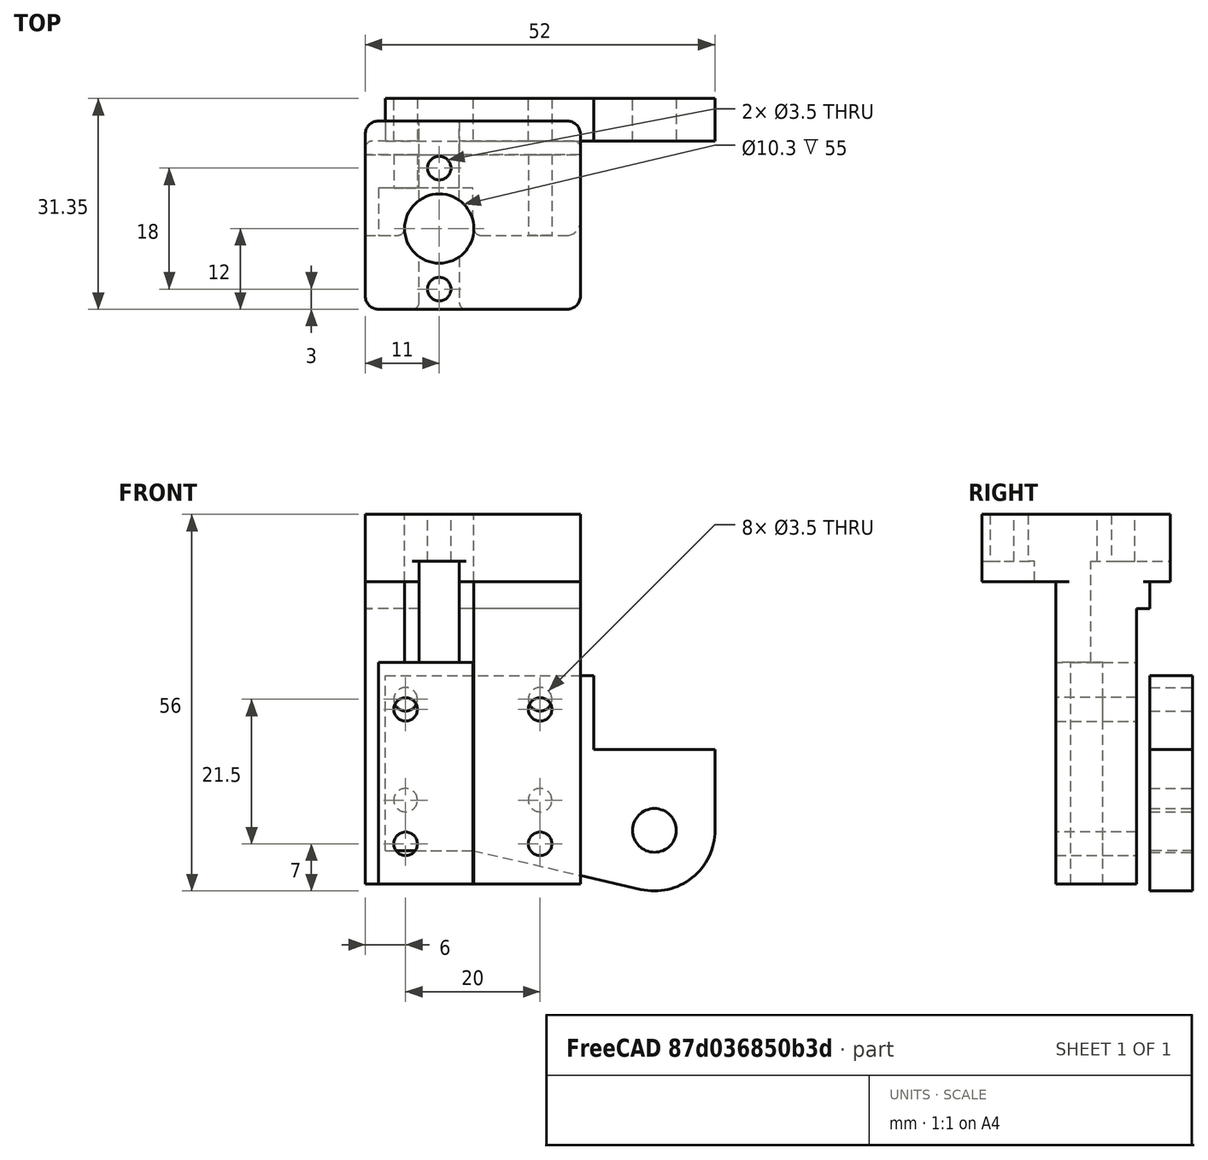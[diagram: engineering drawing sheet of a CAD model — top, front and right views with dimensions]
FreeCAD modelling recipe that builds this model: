
FCSTD DOCUMENT  (FreeCAD 0.19R)
Label: ZnutHolder_H
License: All rights reserved
LicenseURL: http://en.wikipedia.org/wiki/All_rights_reserved
objects: Sketcher::SketchObject×9, PartDesign::Pocket×6, PartDesign::Fillet×5, PartDesign::Pad×2, PartDesign::Body×2, Mesh::Feature×1
note: 37 computed .brp shape members not serialized (recipe doc carries the construction recipe); baked Part::Feature solids carry a one-line shape summary decoded from their .brp

FEATURE [Sketcher::SketchObject] Sketch
  FullyConstrained = false
  MapMode = 5
  Placement = pos=(0,0,0) rot=(1,0,0;1.5708rad)
  Support = -> [XZ_Plane]
  sketch-geometry (14):
    g0: Circle CenterX=-10 CenterY=7.5 CenterZ=0 NormalX=0 NormalY=0 NormalZ=1 AngleXU=0 Radius=1.75
    g1: Circle CenterX=10 CenterY=7.5 CenterZ=0 NormalX=0 NormalY=0 NormalZ=1 AngleXU=0 Radius=1.75
    g2: Circle CenterX=-10 CenterY=-7.5 CenterZ=0 NormalX=0 NormalY=0 NormalZ=1 AngleXU=0 Radius=1.75
    g3: Circle CenterX=10 CenterY=-7.5 CenterZ=0 NormalX=0 NormalY=0 NormalZ=1 AngleXU=0 Radius=1.75
    g4: LineSegment StartX=-13 StartY=11 StartZ=0 EndX=18 EndY=11 EndZ=0
    g5: LineSegment StartX=18 StartY=11 StartZ=0 EndX=18 EndY=0 EndZ=0
    g6: LineSegment StartX=18 StartY=0 StartZ=0 EndX=36 EndY=0 EndZ=0
    g7: LineSegment StartX=36 StartY=0 StartZ=0 EndX=36 EndY=-12 EndZ=0
    g8: LineSegment StartX=-13 StartY=-15 StartZ=0 EndX=-13 EndY=11 EndZ=0
    g9: LineSegment StartX=-13 StartY=-15 StartZ=0 EndX=0 EndY=-15 EndZ=0
    g10: LineSegment StartX=0 StartY=-15 StartZ=0 EndX=24.9743 EndY=-20.7691 EndZ=0
    g11: ArcOfCircle CenterX=27 CenterY=-12 CenterZ=0 NormalX=0 NormalY=0 NormalZ=1 AngleXU=0 Radius=9 StartAngle=4.48537 EndAngle=6.28319
    g12: Circle CenterX=27 CenterY=-12 CenterZ=0 NormalX=0 NormalY=0 NormalZ=1 AngleXU=0 Radius=3.25
    g13: LineSegment StartX=19 StartY=18.0628 StartZ=0 EndX=19 EndY=-24.6673 EndZ=0
  constraints (37):
    c: Symmetric(g0,g1,g-2)
    c: Symmetric(g3,g2,g-2)
    c: Symmetric(g3,g1,g-1)
    c: Diameter(g0) = 3.5
    c: Equal(g0,g1)
    c: Equal(g0,g2)
    c: Equal(g0,g3)
    c: Distance(g1,g0) = 20
    c: Distance(g3,g1) = 15
    c: Horizontal(g4)
    c: Coincident(g4,g5)
    c: Vertical(g5)
    c: Coincident(g5,g6)
    c: Horizontal(g6)
    c: Coincident(g6,g7)
    c: Vertical(g7)
    c: Vertical(g8)
    c: DistanceX(g4) = 18
    c: DistanceX(g4) = -13
    c: Coincident(g8,g9)
    c: PointOnObject(g9,g-2)
    c: Horizontal(g9)
    c: Coincident(g9,g10)
    c: Tangent(g7,g11) = 1.5708
    c: Coincident(g11,g7)
    c: Tangent(g11,g10) = -1.5708
    c: Coincident(g12,g11)
    c: Diameter(g12) = 6.5
    c: Diameter(g11) = 18
    c: Vertical(g13)
    c: DistanceX(g13) = 19
    c: Distance(g11,g13) = 8
    c: Distance(g11,g6) = 12
    c: PointOnObject(g5,g-1)
    c: Coincident(g8,g4)
    c: DistanceY(g4) = 11
    c: DistanceY(g8) = -15
FEATURE [PartDesign::Pad] Pad
  Direction = (1,1,1)
  Length = 6.35
  Length2 = 100
  Placement = pos=(0,0,0) rot=(1,0,0;1.5708rad)
  Profile = -> Sketch
  Type = 0
FEATURE [PartDesign::Body] Body  label="Tab"
  Group = -> [Sketch,Pad]
  Origin = -> Origin
  Placement = pos=(0,6.35,0) rot=(0,0,1;0rad)
  Tip = -> Pad
FEATURE [Sketcher::SketchObject] Sketch005  label="body"
  FullyConstrained = true
  MapMode = 5
  Placement = pos=(0,0,0) rot=(0.57735,0.57735,0.57735;2.0944rad)
  Support = -> [YZ_Plane001]
  sketch-geometry (8):
    g0: LineSegment StartX=0 StartY=-20 StartZ=0 EndX=0 EndY=25 EndZ=0
    g1: LineSegment StartX=0 StartY=25 StartZ=0 EndX=3 EndY=25 EndZ=0
    g2: LineSegment StartX=3 StartY=25 StartZ=0 EndX=3 EndY=35 EndZ=0
    g3: LineSegment StartX=3 StartY=35 StartZ=0 EndX=-25 EndY=35 EndZ=0
    g4: LineSegment StartX=-25 StartY=35 StartZ=0 EndX=-25 EndY=25 EndZ=0
    g5: LineSegment StartX=-25 StartY=25 StartZ=0 EndX=-14 EndY=25 EndZ=0
    g6: LineSegment StartX=-14 StartY=25 StartZ=0 EndX=-14 EndY=-20 EndZ=0
    g7: LineSegment StartX=-14 StartY=-20 StartZ=0 EndX=0 EndY=-20 EndZ=0
  constraints (24):
    c: PointOnObject(g0,g-2)
    c: PointOnObject(g0,g-2)
    c: Coincident(g0,g1)
    c: Coincident(g1,g2)
    c: Vertical(g2)
    c: Coincident(g2,g3)
    c: Horizontal(g3)
    c: Coincident(g3,g4)
    c: Vertical(g4)
    c: Coincident(g4,g5)
    c: Horizontal(g5)
    c: Coincident(g5,g6)
    c: Vertical(g6)
    c: Coincident(g6,g7)
    c: Coincident(g7,g0)
    c: Horizontal(g7)
    c: Distance(g4) = 10
    c: DistanceY(g2) = 35
    c: DistanceX(g4) = -25
    c: Distance(g7) = 14
    c: DistanceY(g0) = -20
    c: DistanceX(g2) = 3
    c: Horizontal(g1)
    c: Distance(g2) = 10
FEATURE [PartDesign::Pad] Pad001
  Direction = (1,1,1)
  Length = 16
  Length2 = 16
  Placement = pos=(0,0,0) rot=(0.57735,0.57735,0.57735;2.0944rad)
  Profile = -> Sketch005
  Type = 4
FEATURE [Sketcher::SketchObject] Sketch011  label="Carriage"
  FullyConstrained = false
  MapMode = 5
  Placement = pos=(0,0,0) rot=(1,0,0;1.5708rad)
  Support = -> [XZ_Plane001]
  sketch-geometry (4):
    g0: LineSegment StartX=-19.4447 StartY=17.5 StartZ=0 EndX=25.2288 EndY=17.5 EndZ=0
    g1: LineSegment StartX=25.2288 StartY=17.5 StartZ=0 EndX=25.2288 EndY=-17.5 EndZ=0
    g2: LineSegment StartX=25.2288 StartY=-17.5 StartZ=0 EndX=-19.4447 EndY=-17.5 EndZ=0
    g3: LineSegment StartX=-19.4447 StartY=-17.5 StartZ=0 EndX=-19.4447 EndY=17.5 EndZ=0
  constraints (10):
    c: Coincident(g0,g1)
    c: Coincident(g1,g2)
    c: Coincident(g2,g3)
    c: Coincident(g3,g0)
    c: Horizontal(g0)
    c: Horizontal(g2)
    c: Vertical(g1)
    c: Vertical(g3)
    c: DistanceY(g0) = 17.5
    c: Distance(g1) = 35
FEATURE [Sketcher::SketchObject] Sketch012  label="NutHole"
  FullyConstrained = true
  MapMode = 5
  Placement = pos=(-6e-14,3.5e-14,35) rot=(0,0,-1;1.5708rad)
  sketch-geometry (1):
    g0: Circle CenterX=13 CenterY=-5 CenterZ=0 NormalX=0 NormalY=0 NormalZ=1 AngleXU=0 Radius=5.15
  constraints (3):
    c: Diameter(g0) = 10.3
    c: DistanceY(g0) = -5
    c: DistanceX(g0) = 13
FEATURE [Sketcher::SketchObject] Sketch013  label="Nutscrews"
  FullyConstrained = true
  MapMode = 5
  Placement = pos=(-7.2e-14,3.9e-14,35) rot=(0,0,-1;1.5708rad)
  sketch-geometry (2):
    g0: Circle CenterX=4 CenterY=-5 CenterZ=0 NormalX=0 NormalY=0 NormalZ=1 AngleXU=0 Radius=1.75
    g1: Circle CenterX=22 CenterY=-5 CenterZ=0 NormalX=0 NormalY=0 NormalZ=1 AngleXU=0 Radius=1.75
  constraints (6):
    c: DistanceY(g1) = -5
    c: DistanceY(g0) = -5
    c: DistanceX(g1) = 22
    c: DistanceX(g0) = 4
    c: Diameter(g1) = 3.5
    c: Equal(g1,g0)
FEATURE [Sketcher::SketchObject] Sketch014
  ExternalGeometry = -> [Pad001]
  FullyConstrained = true
  MapMode = 5
  Placement = pos=(-1.1e-14,-25,5.5e-15) rot=(-0.57735,-0.57735,0.57735;4.18879rad)
  Support = -> [Pad001]
  sketch-geometry (4):
    g0: LineSegment StartX=-28 StartY=-2 StartZ=0 EndX=-13 EndY=-2 EndZ=0
    g1: LineSegment StartX=-13 StartY=-2 StartZ=0 EndX=-13 EndY=-8 EndZ=0
    g2: LineSegment StartX=-13 StartY=-8 StartZ=0 EndX=-28 EndY=-8 EndZ=0
    g3: LineSegment StartX=-28 StartY=-8 StartZ=0 EndX=-28 EndY=-2 EndZ=0
  constraints (12):
    c: Coincident(g0,g1)
    c: Coincident(g1,g2)
    c: Coincident(g2,g3)
    c: Coincident(g3,g0)
    c: Horizontal(g0)
    c: Horizontal(g2)
    c: Vertical(g1)
    c: Vertical(g3)
    c: Distance(g0,g-3) = 7
    c: Distance(g1) = 6
    c: DistanceY(g0) = -2
    c: Distance(g0) = 15
FEATURE [PartDesign::Pocket] Pocket
  BaseFeature = -> Pad001
  Length = 5
  Length2 = 100
  Placement = pos=(0,0,0) rot=(0.57735,0.57735,0.57735;2.0944rad)
  Profile = -> Sketch014
  Type = 1
FEATURE [PartDesign::Pocket] Pocket001
  BaseFeature = -> Pocket
  Length = 5
  Length2 = 100
  Placement = pos=(0,0,0) rot=(0.57735,0.57735,0.57735;2.0944rad)
  Profile = -> Sketch012
  Type = 1
FEATURE [PartDesign::Pocket] Pocket002
  BaseFeature = -> Pocket001
  Length = 7
  Length2 = 100
  Placement = pos=(0,0,0) rot=(0.57735,0.57735,0.57735;2.0944rad)
  Profile = -> Sketch013
  Type = 0
FEATURE [Sketcher::SketchObject] Sketch008  label="ScrewRelief"
  FullyConstrained = false
  MapMode = 5
  Placement = pos=(5.6e-15,-1.32e-14,-20) rot=(0.707107,0.707107,0;3.14159rad)
  Support = -> [Pocket002]
  sketch-geometry (4):
    g0: LineSegment StartX=-14.9077 StartY=0 StartZ=0 EndX=-7 EndY=0 EndZ=0
    g1: LineSegment StartX=-7 StartY=0 StartZ=0 EndX=-7 EndY=-14 EndZ=0
    g2: LineSegment StartX=-7 StartY=-14 StartZ=0 EndX=-14.9077 EndY=-14 EndZ=0
    g3: LineSegment StartX=-14.9077 StartY=-14 StartZ=0 EndX=-14.9077 EndY=0 EndZ=0
  constraints (11):
    c: Coincident(g0,g1)
    c: Coincident(g1,g2)
    c: Coincident(g2,g3)
    c: Coincident(g3,g0)
    c: Horizontal(g0)
    c: Horizontal(g2)
    c: Vertical(g1)
    c: Vertical(g3)
    c: Distance(g1) = 14
    c: DistanceY(g0) = 0
    c: DistanceX(g1) = -7
FEATURE [PartDesign::Pocket] Pocket003
  BaseFeature = -> Pocket002
  Length = 33
  Length2 = 100
  Placement = pos=(0,0,0) rot=(0.57735,0.57735,0.57735;2.0944rad)
  Profile = -> Sketch008
  Type = 0
FEATURE [Sketcher::SketchObject] Sketch007  label="ScrewHoles_rail"
  FullyConstrained = true
  MapMode = 5
  Placement = pos=(-1.08e-14,-14,3.1e-15) rot=(-0.57735,-0.57735,0.57735;4.18879rad)
  Support = -> [Pocket003]
  sketch-geometry (8):
    g0: Circle CenterX=-6 CenterY=10 CenterZ=0 NormalX=0 NormalY=0 NormalZ=1 AngleXU=0 Radius=1.75
    g1: Circle CenterX=14 CenterY=10 CenterZ=0 NormalX=0 NormalY=0 NormalZ=1 AngleXU=0 Radius=1.75
    g2: Circle CenterX=-6 CenterY=-10 CenterZ=0 NormalX=0 NormalY=0 NormalZ=1 AngleXU=0 Radius=1.75
    g3: Circle CenterX=14 CenterY=-10 CenterZ=0 NormalX=0 NormalY=0 NormalZ=1 AngleXU=0 Radius=1.75
    g4: LineSegment StartX=-6 StartY=10 StartZ=0 EndX=-6 EndY=-10 EndZ=0
    g5: LineSegment StartX=-6 StartY=-10 StartZ=0 EndX=14 EndY=-10 EndZ=0
    g6: LineSegment StartX=14 StartY=-10 StartZ=0 EndX=14 EndY=10 EndZ=0
    g7: LineSegment StartX=14 StartY=10 StartZ=0 EndX=-6 EndY=10 EndZ=0
  constraints (19):
    c: Diameter(g0) = 3.5
    c: Equal(g0,g1)
    c: Equal(g0,g2)
    c: Equal(g0,g3)
    c: Coincident(g4,g0)
    c: Coincident(g4,g2)
    c: Coincident(g4,g5)
    c: Coincident(g5,g3)
    c: Coincident(g5,g6)
    c: Coincident(g6,g1)
    c: Coincident(g6,g7)
    c: Coincident(g7,g4)
    c: Equal(g4,g6)
    c: Equal(g7,g5)
    c: Distance(g7) = 20
    c: Distance(g6) = 20
    c: Perpendicular(g6,g5)
    c: Symmetric(g1,g3,g-1)
    c: DistanceX(g0) = -6
FEATURE [PartDesign::Pocket] Pocket004
  BaseFeature = -> Pocket003
  Length = 5
  Length2 = 100
  Placement = pos=(0,0,0) rot=(0.57735,0.57735,0.57735;2.0944rad)
  Profile = -> Sketch007
  Type = 1
FEATURE [Sketcher::SketchObject] Sketch015  label="backpocket"
  ExternalGeometry = -> [Pocket004]
  FullyConstrained = true
  MapMode = 5
  Placement = pos=(0,-1.6e-14,0) rot=(0.57735,0.57735,0.57735;4.18879rad)
  Support = -> [Pocket004]
  sketch-geometry (4):
    g0: LineSegment StartX=-29.47 StartY=20 StartZ=0 EndX=21 EndY=20 EndZ=0
    g1: LineSegment StartX=21 StartY=20 StartZ=0 EndX=21 EndY=-20 EndZ=0
    g2: LineSegment StartX=21 StartY=-20 StartZ=0 EndX=-29.47 EndY=-20 EndZ=0
    g3: LineSegment StartX=-29.47 StartY=-20 StartZ=0 EndX=-29.47 EndY=20 EndZ=0
  constraints (11):
    c: Coincident(g0,g1)
    c: Coincident(g1,g2)
    c: Coincident(g2,g3)
    c: Coincident(g3,g0)
    c: Horizontal(g0)
    c: Horizontal(g2)
    c: Vertical(g1)
    c: Distance(g3) = 40
    c: Symmetric(g2,g0,g-1)
    c: Distance(g0) = 50.47
    c: Distance(g-3,g1) = 15
FEATURE [PartDesign::Pocket] Pocket005
  BaseFeature = -> Pocket004
  Length = 2
  Length2 = 100
  Placement = pos=(0,0,0) rot=(0.57735,0.57735,0.57735;2.0944rad)
  Profile = -> Sketch015
  Type = 0
FEATURE [PartDesign::Fillet] Fillet
  Base = -> Pocket005 [Edge58,Edge12,Edge10,Edge51]
  BaseFeature = -> Pocket005
  Placement = pos=(0,0,0) rot=(0.57735,0.57735,0.57735;2.0944rad)
  Radius = 2
  SupportTransform = false
FEATURE [PartDesign::Fillet] Fillet001
  Base = -> Fillet [Edge70,Edge21]
  BaseFeature = -> Fillet
  Placement = pos=(0,0,0) rot=(0.57735,0.57735,0.57735;2.0944rad)
  Radius = 1
  SupportTransform = false
FEATURE [PartDesign::Fillet] Fillet002
  Base = -> Fillet001 [Edge46,Edge42]
  BaseFeature = -> Fillet001
  Placement = pos=(0,0,0) rot=(0.57735,0.57735,0.57735;2.0944rad)
  Radius = 1
  SupportTransform = false
FEATURE [PartDesign::Fillet] Fillet003
  Base = -> Fillet002 [Edge32,Edge125]
  BaseFeature = -> Fillet002
  Placement = pos=(0,0,0) rot=(0.57735,0.57735,0.57735;2.0944rad)
  Radius = 1
  SupportTransform = false
FEATURE [PartDesign::Fillet] Fillet004
  Base = -> Fillet003 [Edge73]
  BaseFeature = -> Fillet003
  Placement = pos=(0,0,0) rot=(0.57735,0.57735,0.57735;2.0944rad)
  Radius = 2
  SupportTransform = false
FEATURE [PartDesign::Body] Body001  label="LeadScrewMount"
  Group = -> [Sketch005,Pad001,Sketch007,Sketch008,Sketch011,Sketch012,Sketch013,Sketch014,Pocket,Pocket001,Pocket002,Pocket003,Pocket004,Sketch015,Pocket005,Fillet,Fillet001,Fillet002,Fillet003,Fillet004]
  Origin = -> Origin001
  Tip = -> Fillet004
FEATURE [Mesh::Feature] Mesh  label="Fillet004 (Meshed)"
